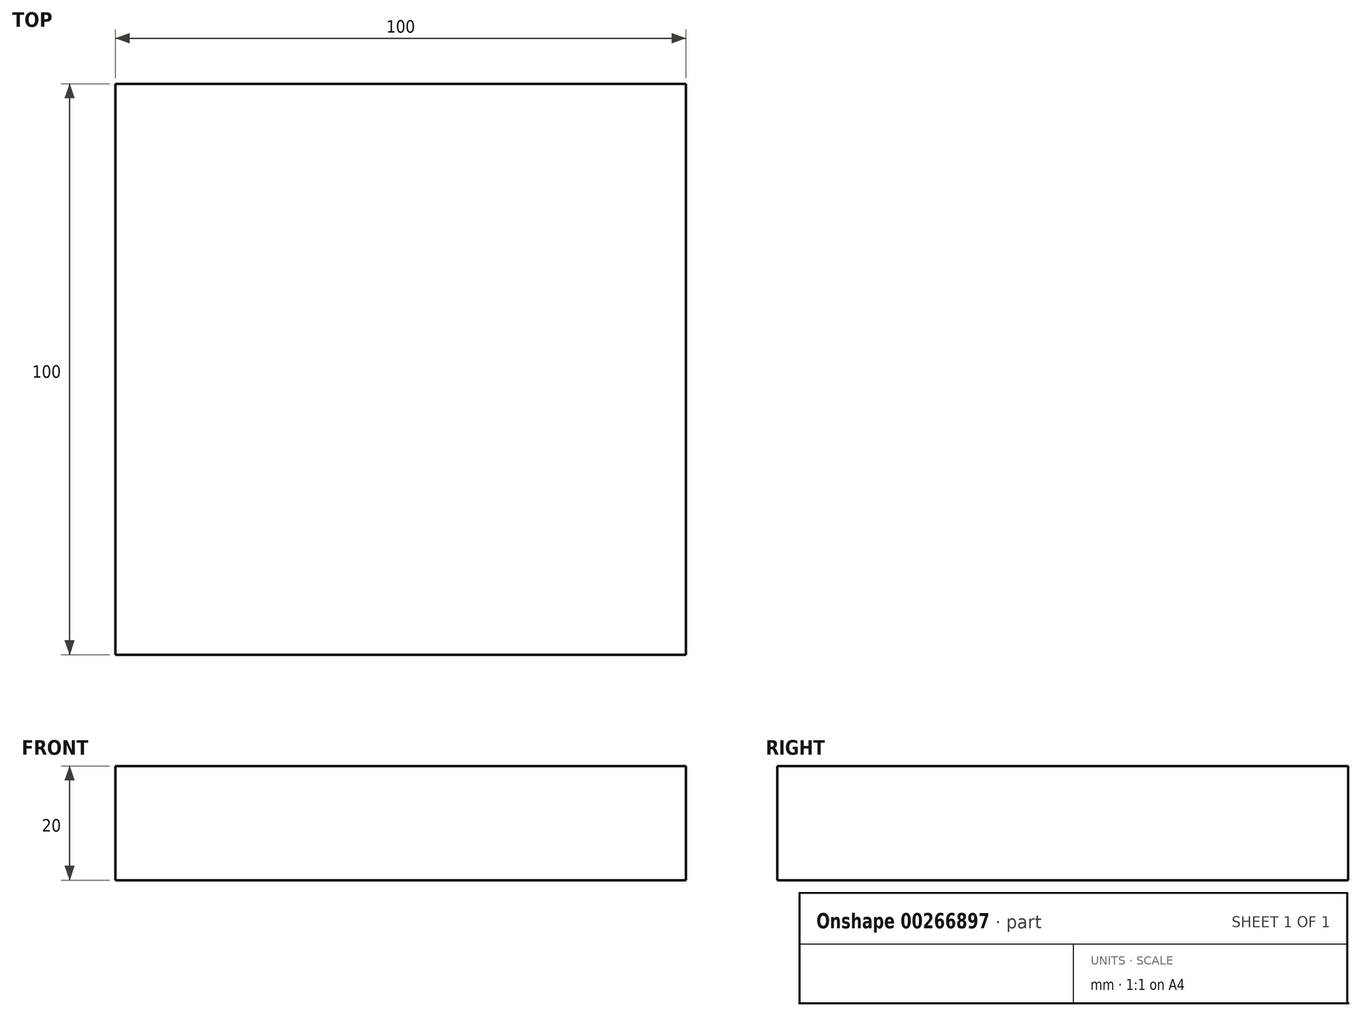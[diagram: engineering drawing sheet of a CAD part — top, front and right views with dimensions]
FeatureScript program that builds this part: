
annotation { "Feature Type Name" : "Feature", "Feature Type Description" : "" }
export const myFeature = defineFeature(function(context is Context, id is Id, definition is map)
    precondition{}
    {
        {
            var Q0;
            Q0=qCreatedBy(makeId("Top.planeOp"),FACE);
            var sketch = newSketch(context, id + "F0", { "sketchPlane" : qUnion([Q0])});
            skLineSegment(sketch, "E0.bottom", {"start": v(50, 50) * mm, "end": v(-50, 50) * mm});
            skLineSegment(sketch, "E0.top", {"start": v(50, -50) * mm, "end": v(-50, -50) * mm});
            skLineSegment(sketch, "E0.left", {"start": v(50, 50) * mm, "end": v(50, -50) * mm});
            skLineSegment(sketch, "E0.right", {"start": v(-50, 50) * mm, "end": v(-50, -50) * mm});
            skPoint(sketch, "E0.middle", {"position": v(0, 0) * mm});
            skSolve(sketch);
        }
        {
            var Q0;
            Q0=qSketchRegion(id+"F0",true);
            extrude(context, id + "F1", {"entities" : qUnion([Q0]), "depth" : 20 * mm});
        }
    });
